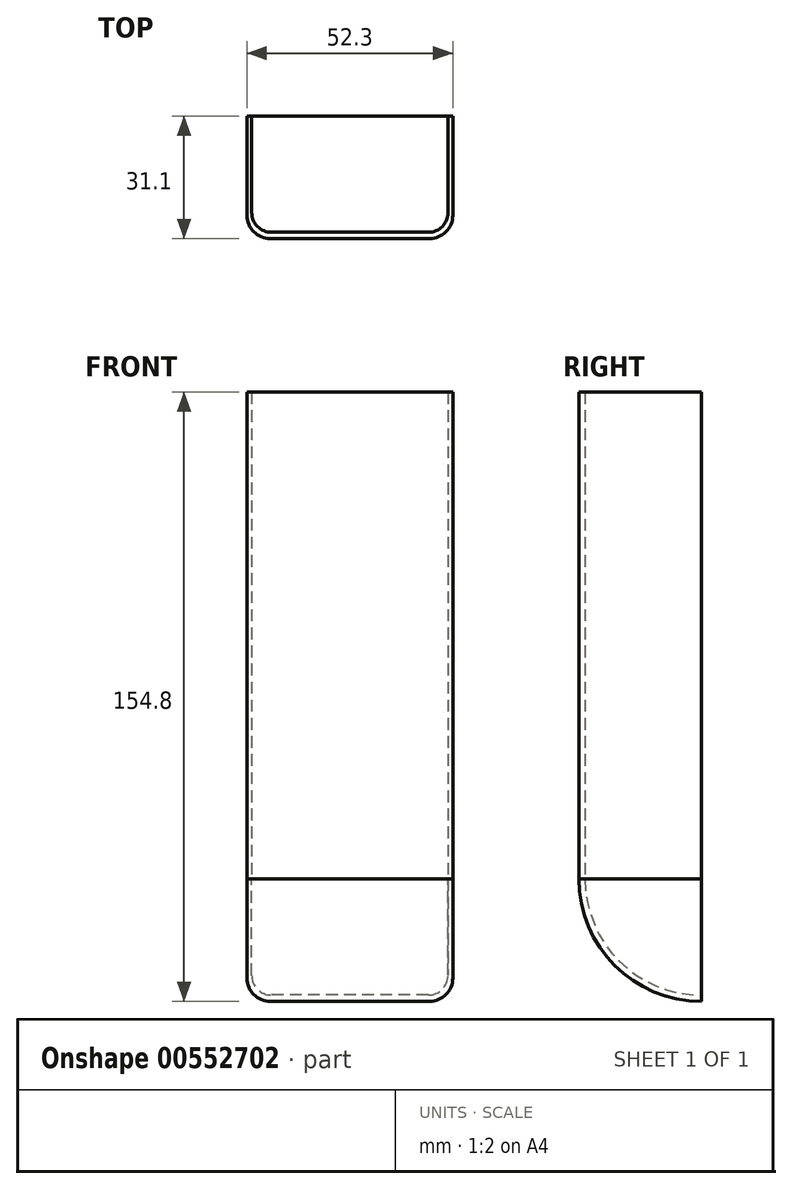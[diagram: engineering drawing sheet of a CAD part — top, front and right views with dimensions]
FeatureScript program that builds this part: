
annotation { "Feature Type Name" : "Feature", "Feature Type Description" : "" }
export const myFeature = defineFeature(function(context is Context, id is Id, definition is map)
    precondition{}
    {
        {
            var Q0;
            Q0=qCreatedBy(makeId("Top.planeOp"),FACE);
            var sketch = newSketch(context, id + "F0", { "sketchPlane" : qUnion([Q0])});
            skLineSegment(sketch, "E0", {"start": v(-55, 43.7) * mm, "end": v(-55, 18.5) * mm});
            skLineSegment(sketch, "E1", {"start": v(-49.1, 12.6) * mm, "end": v(-8.6, 12.6) * mm});
            skLineSegment(sketch, "E2", {"start": v(-2.7, 18.51) * mm, "end": v(-2.7, 43.7) * mm});
            skLineSegment(sketch, "E3", {"start": v(-2.7, 43.7) * mm, "end": v(-3.9, 43.7) * mm});
            skLineSegment(sketch, "E4", {"start": v(-3.9, 43.7) * mm, "end": v(-3.9, 19.23) * mm});
            skLineSegment(sketch, "E5", {"start": v(-8.93, 14.2) * mm, "end": v(-48.77, 14.2) * mm});
            skLineSegment(sketch, "E6", {"start": v(-53.8, 19.23) * mm, "end": v(-53.8, 43.7) * mm});
            skLineSegment(sketch, "E7", {"start": v(-53.8, 43.7) * mm, "end": v(-55, 43.7) * mm});
            skPoint(sketch, "E8.visualSharp", {"position": v(-3.9, 14.2) * mm});
            skArc(sketch, "E8.filletArc", {"start": v(-8.93, 14.2) * mm, "mid": v(-5.37, 15.68) * mm, "end": v(-3.9, 19.23) * mm});
            skPoint(sketch, "E9.visualSharp", {"position": v(-53.8, 14.2) * mm});
            skArc(sketch, "E9.filletArc", {"start": v(-53.8, 19.23) * mm, "mid": v(-52.33, 15.68) * mm, "end": v(-48.77, 14.2) * mm});
            skPoint(sketch, "E10.visualSharp", {"position": v(-2.7, 12.6) * mm});
            skArc(sketch, "E10.filletArc", {"start": v(-8.6, 12.6) * mm, "mid": v(-4.43, 14.33) * mm, "end": v(-2.7, 18.51) * mm});
            skPoint(sketch, "E11.visualSharp", {"position": v(-55, 12.6) * mm});
            skArc(sketch, "E11.filletArc", {"start": v(-55, 18.5) * mm, "mid": v(-53.27, 14.33) * mm, "end": v(-49.1, 12.6) * mm});
            skSolve(sketch);
        }
        {
            var Q0;
            Q0=makeQuery(id+"F0.imprint","IMPRINT",FACE,{"disambiguationData":[TD([[makeQuery(id+"F0.imprint","IMPRINT",EDGE,{"derivedFrom":sQuery(id+"F0.wireOp",EDGE,"E0")}),1.0]])]});
            extrude(context, id + "F1", {"entities" : qUnion([Q0]), "depth" : 5 * mm, "offsetDistance" : 25 * mm});
        }
        {
            var Q0;
            Q0=makeQuery(id+"F1.opExtrude","CAP_FACE",FACE,{"disambiguationData":[OSD([sQuery(id+"F0.wireOp",EDGE,"E0"),sQuery(id+"F0.wireOp",EDGE,"E1"),sQuery(id+"F0.wireOp",EDGE,"E2"),sQuery(id+"F0.wireOp",EDGE,"E3"),sQuery(id+"F0.wireOp",EDGE,"E4"),sQuery(id+"F0.wireOp",EDGE,"E5"),sQuery(id+"F0.wireOp",EDGE,"E6"),sQuery(id+"F0.wireOp",EDGE,"E7"),sQuery(id+"F0.wireOp",EDGE,"E8.filletArc"),sQuery(id+"F0.wireOp",EDGE,"E9.filletArc"),sQuery(id+"F0.wireOp",EDGE,"E10.filletArc"),sQuery(id+"F0.wireOp",EDGE,"E11.filletArc")])],"isStart":false});
            extrude(context, id + "F2", {"entities" : qUnion([Q0]), "operationType" : NewBodyOperationType.ADD, "depth" : 88 * mm, "offsetDistance" : 25 * mm});
        }
        {
            var Q0;
            Q0=makeQuery(id+"F1.opExtrude","CAP_FACE",FACE,{"disambiguationData":[OSD([sQuery(id+"F0.wireOp",EDGE,"E0"),sQuery(id+"F0.wireOp",EDGE,"E1"),sQuery(id+"F0.wireOp",EDGE,"E2"),sQuery(id+"F0.wireOp",EDGE,"E3"),sQuery(id+"F0.wireOp",EDGE,"E4"),sQuery(id+"F0.wireOp",EDGE,"E5"),sQuery(id+"F0.wireOp",EDGE,"E6"),sQuery(id+"F0.wireOp",EDGE,"E7"),sQuery(id+"F0.wireOp",EDGE,"E8.filletArc"),sQuery(id+"F0.wireOp",EDGE,"E9.filletArc"),sQuery(id+"F0.wireOp",EDGE,"E10.filletArc"),sQuery(id+"F0.wireOp",EDGE,"E11.filletArc")])],"isStart":true});
            var sketch = newSketch(context, id + "F3", { "sketchPlane" : qUnion([Q0])});
            skLineSegment(sketch, "E12", {"start": v(-3.9, -19.23) * mm, "end": v(-2.7, -18.51) * mm});
            skLineSegment(sketch, "E13", {"start": v(-53.8, -19.23) * mm, "end": v(-55, -18.5) * mm});
            skSolve(sketch);
        }
        {
            var Q0;
            Q0=makeQuery(id+"F3.imprint","IMPRINT",FACE,{"disambiguationData":[TD([[makeQuery(id+"F3.imprint","IMPRINT",EDGE,{"derivedFrom":sQuery(id+"F3.wireOp",EDGE,"E12")}),1.0]])]});
            var Q1;
            Q1=makeQuery(id+"F3.imprint","IMPRINT",FACE,{"disambiguationData":[TD([[makeQuery(id+"F3.imprint","IMPRINT",EDGE,{"derivedFrom":sQuery(id+"F3.wireOp",EDGE,"E12")}),-1.0]])]});
            var Q2;
            Q2=makeQuery(id+"F3.imprint","IMPRINT",FACE,{"disambiguationData":[TD([[makeQuery(id+"F3.imprint","IMPRINT",EDGE,{"derivedFrom":sQuery(id+"F3.wireOp",EDGE,"E13")}),1.0]])]});
            var Q3;
            Q3=makeQuery(id+"F1.opExtrude","CAP_EDGE",EDGE,{"disambiguationData":[OSD([sQuery(id+"F0.wireOp",EDGE,"E3")])],"isStart":true});
            revolve(context, id + "F4", {"entities" : qUnion([Q0, Q1, Q2]), "axis" : qUnion([Q3]), "revolveType" : RevolveType.ONE_DIRECTION, "oppositeDirection" : true, "angle" : 90 * degree});
        }
        {
            var Q0;
            Q0=makeQuery(id+"F2.opExtrude","CAP_FACE",FACE,{"disambiguationData":[OSD([sQuery(id+"F0.wireOp",EDGE,"E0"),sQuery(id+"F0.wireOp",EDGE,"E1"),sQuery(id+"F0.wireOp",EDGE,"E2"),sQuery(id+"F0.wireOp",EDGE,"E3"),sQuery(id+"F0.wireOp",EDGE,"E4"),sQuery(id+"F0.wireOp",EDGE,"E5"),sQuery(id+"F0.wireOp",EDGE,"E6"),sQuery(id+"F0.wireOp",EDGE,"E7"),sQuery(id+"F0.wireOp",EDGE,"E8.filletArc"),sQuery(id+"F0.wireOp",EDGE,"E9.filletArc"),sQuery(id+"F0.wireOp",EDGE,"E10.filletArc"),sQuery(id+"F0.wireOp",EDGE,"E11.filletArc")])],"isStart":false});
            extrude(context, id + "F5", {"entities" : qUnion([Q0]), "operationType" : NewBodyOperationType.ADD, "depth" : 30.7 * mm, "offsetDistance" : 25 * mm});
        }
    });
